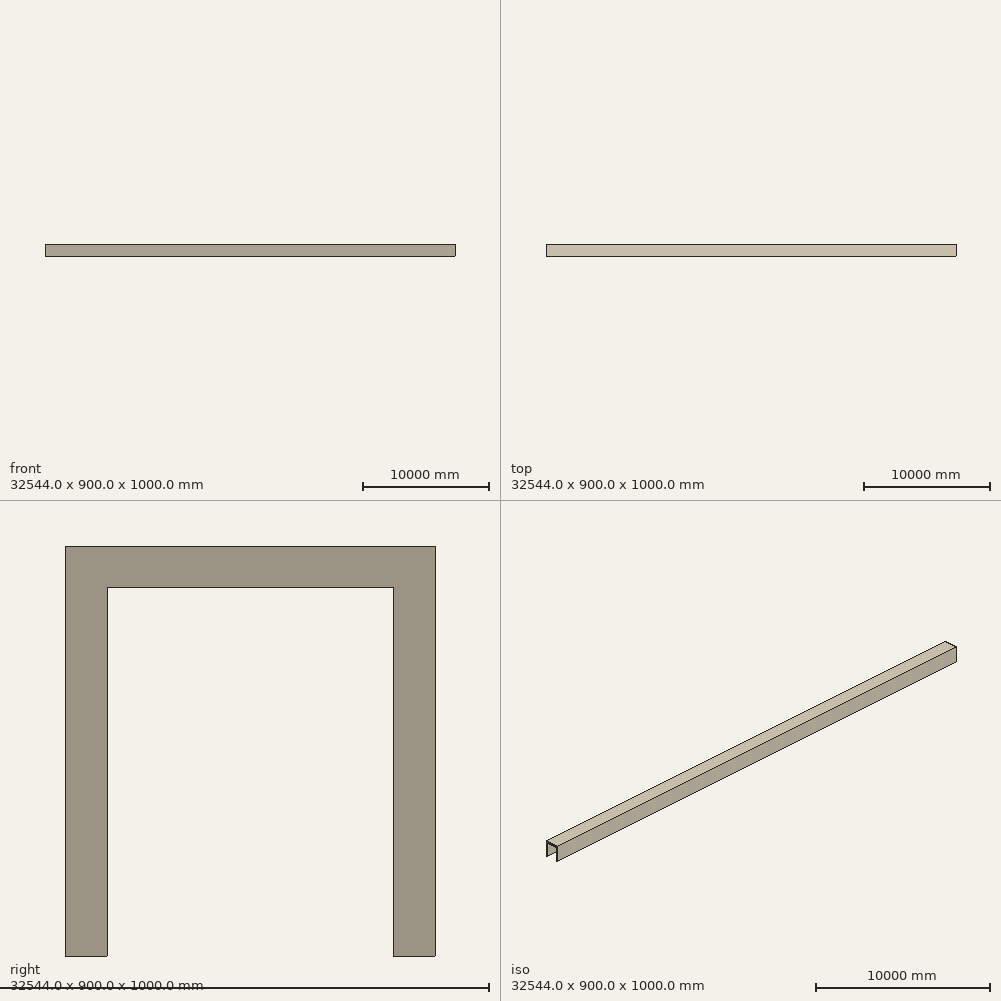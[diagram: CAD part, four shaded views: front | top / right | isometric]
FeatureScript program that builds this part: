
annotation { "Feature Type Name" : "Feature", "Feature Type Description" : "" }
export const myFeature = defineFeature(function(context is Context, id is Id, definition is map)
    precondition{}
    {
        {
            var Q0;
            Q0=qCreatedBy(makeId("Right.planeOp"),FACE);
            var sketch = newSketch(context, id + "F0", { "sketchPlane" : qUnion([Q0])});
            skLineSegment(sketch, "E0.bottom", {"start": v(0, 0) * mm, "end": v(900, 0) * mm});
            skLineSegment(sketch, "E0.top", {"start": v(0, -1000) * mm, "end": v(100, -1000) * mm});
            skLineSegment(sketch, "E0.left", {"start": v(0, 0) * mm, "end": v(0, -1000) * mm});
            skLineSegment(sketch, "E0.right", {"start": v(900, 0) * mm, "end": v(900, -1000) * mm});
            skLineSegment(sketch, "E1.top", {"start": v(100, -100) * mm, "end": v(800, -100) * mm});
            skLineSegment(sketch, "E1.left", {"start": v(100, -1000) * mm, "end": v(100, -100) * mm});
            skLineSegment(sketch, "E1.right", {"start": v(800, -1000) * mm, "end": v(800, -100) * mm});
            skLineSegment(sketch, "E2.trimOffspring", {"start": v(800, -1000) * mm, "end": v(900, -1000) * mm});
            skSolve(sketch);
        }
        {
            var Q0;
            Q0 = qSketchRegion(id + "F0", true);
            extrude(context, id + "F1", {"entities" : qUnion([Q0]), "depth" : 32544 * mm});
        }
    });
